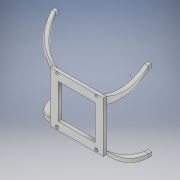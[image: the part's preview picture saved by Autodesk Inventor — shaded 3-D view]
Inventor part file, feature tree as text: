
AUTODESK INVENTOR PART (.ipt)
format: ipt  version: 2019 (Build 230136000, 136)  size: 332,288 bytes
history: native  units: mm
features: sketch x11, extrude x4, other x3, projected_geometry x3, loft x2, mirror x2
ambient origin geometry x8: Origin, YZ Plane, XZ Plane, XY Plane, X Axis, Y Axis, Z Axis, Center Point
bodies: Body1 (feature_tree)
feature tree (25):
  other  "Bryła1"
  sketch  "Szkic1"
  other  "Płaszczyzna konstrukcyjna2"
  other  "Płaszczyzna konstrukcyjna3"
  sketch  "Szkic2"
  sketch  "Szkic3"
  sketch  "Szkic4"
  sketch  "Szkic5"
  sketch  "Szkic6"
  loft  "Wyciągnięcie złożone1"
  loft  "Wyciągnięcie złożone2"
  extrude  "Wyciągnięcie proste1"  Depth=20.0mm
  extrude  "Wyciągnięcie proste2"  TaperAngle=0.0deg  [1 undecoded]
  mirror  "Odbij1"
  sketch  "Szkic10"
  extrude  "Wyciągnięcie proste3"  Depth=35.0mm
  extrude  "Wyciągnięcie proste4"  Depth=5.0mm
  mirror  "Odbij2"
  sketch  "Szkic7"
  sketch  "Szkic8"
  sketch  "Szkic9"
  projected_geometry  "Pętla rzutowana1"
  projected_geometry  "Pętla rzutowana2"
  projected_geometry  "Pętla rzutowana3"
  sketch  "Szkic11"
note: 1 required parameter value undecoded (feature->parameter linkage not recoverable at this tier; creation-order binding heuristic only, values carry confidence <= 0.55)
